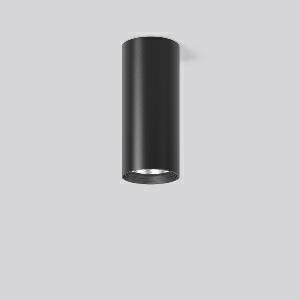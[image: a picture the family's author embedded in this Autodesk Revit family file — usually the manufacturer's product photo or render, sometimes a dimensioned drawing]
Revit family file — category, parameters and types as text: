
# Revit family: heledon_mini_a_931208_003_2_76_b4dd
name_source: partatom
category: Lighting Fixtures
units: mm (PartAtom-declared; Revit-internal decimal feet)

## family parameters
Cut with Voids When Loaded = No
Host = Face
Light Source = No
Part Type = Normal
Room Calculation Point = No
Round Connector Dimension = Use Diameter
Shared = No

## types (1)
- HELEDON mini A (1 x LED Modul 927, 3400 lm, 2700)
    Apparent Load = 29 VA
    Approval mark = CE
    CIE Flux Codes = 100 100 100 100 100
    Color Rendering = 92
    Color Temperature = 2700
    Default Elevation = 1800 mm
    Description = Series: HELEDON mini
Cylindrical surface-mounted downlight. Housing: die-cast aluminium, powder-coated. Internal ceiling frame polycarbonate with bayonet mounting. Black plastic ring and recessed LED to prevent glare from the side. Optical assembly with reflector made of MIRO-Silver with 98% total light reflection for outstanding efficiency - can be changed without tools. Best colour rendering index Ra>90. Suitable for Ceiling mounting. Easy installation with a separate ceiling frame with bayonet mounting and plug connection. Driver integrated. Connected via plug-in connector. High quality converter without flickering and stroboscopic effect. The following accessories can be mounted without use of tools: interchangeable lenses, decorative glasses, honeycomb louvre, clear and frosted diffusers, white interchangeable plastic ring. 
Colour: deep black, matt (RAL 9005)
Diameter: 87 mm
Height: 197 mm
Lamp: LED
Socket: without socket
Colour temperature: 2700K
Colour rendering index (CRI): 92
System power: 29 W
Rated luminous flux: 3400 lm
Luminous efficiency: 117 lm/W
Control gear: Converter, dimmable, DALI
Protection class: I
Type of protection: IP 20
    Height = 197 mm
    Lamp = 1 x LED Modul 927
    Lamp Light Flux = 3400 lm
    Lamp count = 1
    Length = 87 mm
    Lifetime = 50000 h
    Luminous efficacy = 117 lm/W
    Manufacturer = RZB
    ModVariant = No
    Model = 931208.003.2.76
    Mounting Place = Ceiling
    Mounting Type = Surface mounted
    Number of Poles = 1
    OnlyDefault = Yes
    Power Factor = 1
    Product Name = HELEDON mini A
    Product group = Surface mounted downlights
    ProductGroupID = 302
    Protection Class = Protection class I
    Protection Degree = IP 20
    RLX_Detail_Level = 1
    RLX_Emergency_Light_Flux = 0 lm
    RLX_Emergency_Type = 0
    RLX_Emergency_Type_DB = No
    RlxData = <blob elided: 105933 chars, md5=4d7b8aa9>
    Socket = socket
    Standby Power = 0 W
    System Light Flux = 3400 lm
    System Power = 29 W
    Type Comments = Product without accessories
    Type Image = 931188.003.jpg
    URL = http://relux.com
    VarID = ---
    Voltage = 230 V
    Voltage Range = 220-240 V
    Weight = 0.00 kg
    Width = 0 mm  [stored 0 ft]

note: [stored X ft] marks values corroborated as IEEE doubles in the binary element streams (Revit-internal decimal feet)

## geometry (parser evidence)
native form markers: Blend x4, Sweep x10
no freeform markers — native parametric forms only
